# Revit family: Geberit ONE çanak lavabo, kabuk şekilli, yatay çıkış_PRO_2123164
name_source: partatom
category: Plumbing Fixtures
units: mm (PartAtom-declared; Revit-internal decimal feet)

## family parameters
Always vertical = Yes
Cut with Voids When Loaded = No
OmniClass Number = 23.45.05.21
OmniClass Title = Plumbing Fixtures - Sanitary Disposal Units
Part Type = Normal
Room Calculation Point = Yes
Round Connector Dimension = Use Diameter
Shared = No
Work Plane-Based = No

## types (2) — shared parameters
Application purposes = Lavabo plakalarının üzerine montaj için
Application range = Plumbing fixture
BIM Content Version = GEB MG 1.2
BIM Content revision date = 2020.05.18
Brand = Geberit
CW Connection = Yes
Characteristics = Yatay çıkış
Görünmez taşmalık fonksiyonu
Çekme kolu ile çalıştırma
Entegre saç süzgeci ile
Optimum akış tutumu sayesinde hijyenik
Perdahlı alt ve arka yüzey
Description = Geberit ONE çanak lavabo, kabuk şekilli, yatay çıkış
EAN code basic data = 4025410594020
GEB_culture = tr-TR
GEB_generic_description = Bathroom collection
GEB_generic_manufacturer = generic
GEB_pimversion = 23.02.17
GEB_processing_type = T
GEB_reference = PRO_2123164
GEB_translations = {"ATT_10673":"EAN code basic data","ATT_10882":"Malzeme","ATT_459792":"Renk / Yüzey","applicationPurposes":"Application purposes","application_range":"Application range","brandName":"Brand","characteristics":"Characteristics","content_creator":"BIM Content creator","content_date_changed":"BIM Content revision date","content_version":"BIM Content Version","key 1000":"Article number key","name":"Name","productBrand":"Product brand","scopeOfDelivery":"Scope of delivery","type":"Type","fixed_material":"Main material"}
HW Connection = No
IfcDescription = Geberit ONE çanak lavabo, kabuk şekilli, yatay çıkış
IfcExportAs = IfcSanitaryTerminal
LOD300 = No
LOD400 = Yes
Main material = Geberit, Plastic, Opaque white
Malzeme = Seramik
Manufacturer = Geberit
Name = Geberit ONE çanak lavabo, kabuk şekilli, yatay çıkış
Renk / Yüzey = Lavabo: beyaz / KeraTect<br/>Kaplama: parlak beyaz
Scope of delivery = Lavabo
Tarak eklentili tahliye paneli, manyetik sabitleme
Lavabo bağlantısı ve koku sifonu, yer tasarruflu model
Sabitleme malzemesi
Vent Connection = No
Waste Connection = Yes
outlet_flow = 0.0 L/s
zero-valued in all types: Default Elevation

## per-type parameters (varying)
| type | 505050_0_view | 505051_0_view | Article number key |
| 505.050.00.1 Geberit ONE çanak lavabo, kabuk şekilli, yatay çıkış | Yes | No | 505.050.00.1 |
| 505.051.00.1 Geberit ONE çanak lavabo, kabuk şekilli, yatay çıkış | No | Yes | 505.051.00.1 |

## geometry (parser evidence)
native form markers: Blend x8, Sweep x18
no freeform markers — native parametric forms only
